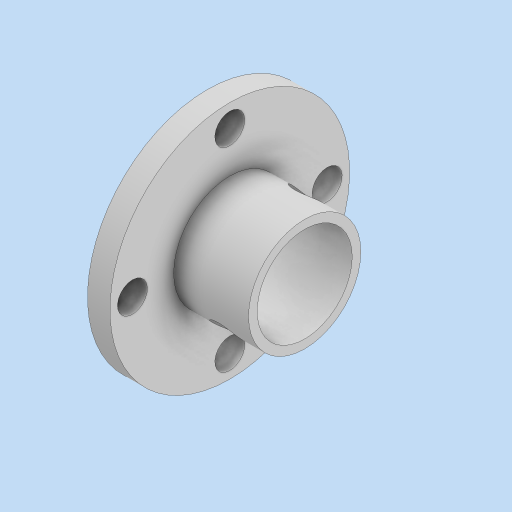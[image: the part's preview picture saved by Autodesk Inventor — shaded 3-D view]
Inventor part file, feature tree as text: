
AUTODESK INVENTOR PART (.ipt)
format: ipt  version: 2024 (Build 280153000, 153)  size: 173,056 bytes
history: native  units: in
note: dims shown in document units (in); Inventor stores cm internally (conversion verified against a paired STEP export)
features: extrude x3, sketch x3, projected_geometry x2, plane x1
ambient origin geometry x8: Origin, YZ Plane, XZ Plane, XY Plane, X Axis, Y Axis, Z Axis, Center Point
bodies: Solid1 (feature_tree)
feature tree (9):
  extrude  "Extrusion1"  Depth=0.1575in
  extrude  "Extrusion2"  Depth=0.5118in
  plane  "Work Plane1"
  extrude  "Extrusion3"  Depth=0.3937in
  sketch  "Sketch1"  dims[d0=1.2598in d1=0.1575in]
  sketch  "Sketch2"  dims[d2=1.0236in d3=0.5118in]
  projected_geometry  "Projected Loop1"
  sketch  "Sketch5"  dims[d4=1.5748in d6=360.0deg d8=0.5in d9=0.1181in d10=0.0in d11=0.5906in d12=0.3937in d13=0.0in d14=0.1575in d15=0.1969in d16=0.0in d17=0.0in]
  projected_geometry  "Projected Loop2"
